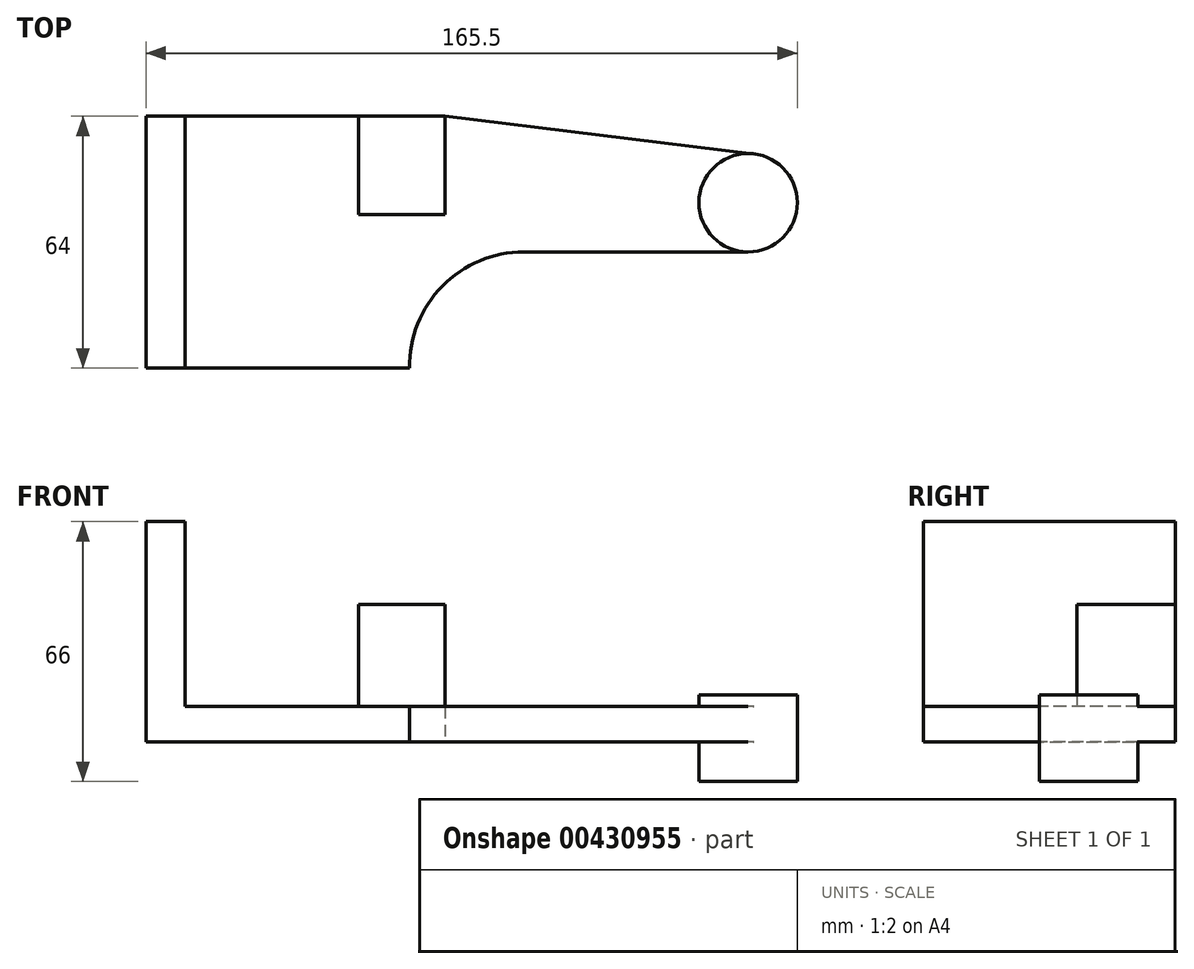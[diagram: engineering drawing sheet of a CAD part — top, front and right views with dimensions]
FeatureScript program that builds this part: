
annotation { "Feature Type Name" : "Feature", "Feature Type Description" : "" }
export const myFeature = defineFeature(function(context is Context, id is Id, definition is map)
    precondition{}
    {
        {
            var Q0;
            Q0=qCreatedBy(makeId("Top.planeOp"),FACE);
            var sketch = newSketch(context, id + "F0", { "sketchPlane" : qUnion([Q0])});
            skLineSegment(sketch, "E0", {"start": v(-153, -42) * mm, "end": v(-153, 22) * mm});
            skLineSegment(sketch, "E1", {"start": v(-153, 22) * mm, "end": v(-77, 22) * mm});
            skLineSegment(sketch, "E2", {"start": v(-77, 22) * mm, "end": v(1.52, 12.4) * mm});
            skLineSegment(sketch, "E3", {"start": v(0, -12.5) * mm, "end": v(-57, -12.5) * mm});
            skCircle(sketch, "E4", {"center": v(0, 0) * mm, "radius": 12.5 * mm});
            skLineSegment(sketch, "E5", {"start": v(-153, -42) * mm, "end": v(-86, -42) * mm});
            skArc(sketch, "E6", {"start": v(-57, -12.5) * mm, "mid": v(-77.69, -21.17) * mm, "end": v(-86, -42) * mm});
            skLineSegment(sketch, "E7", {"start": v(-77, 22) * mm, "end": v(-77, -3) * mm});
            skLineSegment(sketch, "E8", {"start": v(-77, -3) * mm, "end": v(-99, -3) * mm});
            skLineSegment(sketch, "E9", {"start": v(-99, -3) * mm, "end": v(-99, 22) * mm});
            skLineSegment(sketch, "E10", {"start": v(-143, 22) * mm, "end": v(-143, -42) * mm});
            skLineSegment(sketch, "E11", {"start": v(-140, 22) * mm, "end": v(-140, -42) * mm, "construction": true});
            skLineSegment(sketch, "E12", {"start": v(-91, 22) * mm, "end": v(-91, -3) * mm, "construction": true});
            skSolve(sketch);
        }
        {
            var Q0;
            {var subQ1=sQuery(id+"F0.wireOp",EDGE,"E2");Q0=makeQuery(id+"F0.imprint","IMPRINT",FACE,{"disambiguationData":[TD([[makeQuery(id+"F0.imprint","IMPRINT",EDGE,{"derivedFrom":subQ1}),-1.0]])]});}
            extrude(context, id + "F1", {"entities" : qUnion([Q0]), "depth" : 9 * mm});
        }
        {
            var Q0;
            {var subQ0=sQuery(id+"F0.wireOp",EDGE,"E0");Q0=makeQuery(id+"F0.imprint","IMPRINT",FACE,{"disambiguationData":[TD([[makeQuery(id+"F0.imprint","IMPRINT",EDGE,{"derivedFrom":subQ0}),-1.0]])]});}
            extrude(context, id + "F2", {"entities" : qUnion([Q0]), "operationType" : NewBodyOperationType.ADD, "depth" : 56 * mm});
        }
        {
            var Q0;
            {var subQ0=sQuery(id+"F0.wireOp",EDGE,"E7");Q0=makeQuery(id+"F0.imprint","IMPRINT",FACE,{"disambiguationData":[TD([[makeQuery(id+"F0.imprint","IMPRINT",EDGE,{"derivedFrom":subQ0}),-1.0]])]});}
            extrude(context, id + "F3", {"entities" : qUnion([Q0]), "operationType" : NewBodyOperationType.ADD, "depth" : 35 * mm});
        }
        {
            var Q0;
            {var subQ0=sQuery(id+"F0.wireOp",EDGE,"E4");var subQ1=makeQuery(id+"F0.imprint","INTERSECT",VERTEX,{"derivedFrom":[sQuery(id+"F0.wireOp",EDGE,"E2"),subQ0]});Q0=makeQuery(id+"F0.imprint","IMPRINT",FACE,{"disambiguationData":[TD([[makeQuery(id+"F0.imprint","IMPRINT",EDGE,{"disambiguationData":[TD([[subQ1,-1.0]])],"derivedFrom":subQ0}),1.0]])]});}
            extrude(context, id + "F4", {"entities" : qUnion([Q0]), "operationType" : NewBodyOperationType.ADD, "depth" : (9 + 3) * mm, "hasSecondDirection" : true, "secondDirectionOppositeDirection" : true, "secondDirectionDepth" : (22 - 12) * mm});
        }
        {
            var Q0;
            Q0=makeQuery(id+"F3.opExtrude","CAP_FACE",FACE,{"disambiguationData":[OSD([sQuery(id+"F0.wireOp",EDGE,"E1"),sQuery(id+"F0.wireOp",EDGE,"E7"),sQuery(id+"F0.wireOp",EDGE,"E8"),sQuery(id+"F0.wireOp",EDGE,"E9")])],"isStart":false});
            var sketch = newSketch(context, id + "F5", { "sketchPlane" : qUnion([Q0])});
            skLineSegment(sketch, "E13.0", {"start": v(-91, 22) * mm, "end": v(-91, -3) * mm});
            skSolve(sketch);
        }
        {
            var Q0;
            {var subQ0=sQuery(id+"F5.wireOp",EDGE,"E13.0");Q0=makeQuery(id+"F5.imprint","IMPRINT",FACE,{"disambiguationData":[TD([[makeQuery(id+"F5.imprint","IMPRINT",EDGE,{"derivedFrom":subQ0}),1.0]])]});}
            extrude(context, id + "F6", {"entities" : qUnion([Q0]), "operationType" : NewBodyOperationType.ADD, "oppositeDirection" : true, "depth" : (35 - 19) * mm});
        }
    });
